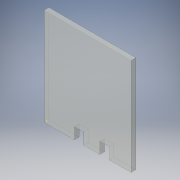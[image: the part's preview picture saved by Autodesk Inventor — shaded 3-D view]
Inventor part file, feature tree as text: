
AUTODESK INVENTOR PART (.ipt)
format: ipt  version: 2016 (Build 200138000, 138)  size: 111,616 bytes
history: native  units: in
note: dims shown in document units (in); Inventor stores cm internally (conversion verified against a paired STEP export)
features: sketch x2, extrude x1
ambient origin geometry x8: Origin, YZ Plane, XZ Plane, XY Plane, X Axis, Y Axis, Z Axis, Center Point
bodies: Solid1 (feature_tree)
feature tree (3):
  sketch  "Sketch1"  dims[d1=10.5in d2=5.125in]
  extrude  "Extrusion1"  Depth=5.125in
  sketch  "Sketch2"  dims[d3=0.875in d4=1.0in d5=0.875in d6=1.0in d7=1.25in d8=0.5in d9=0.0in]
